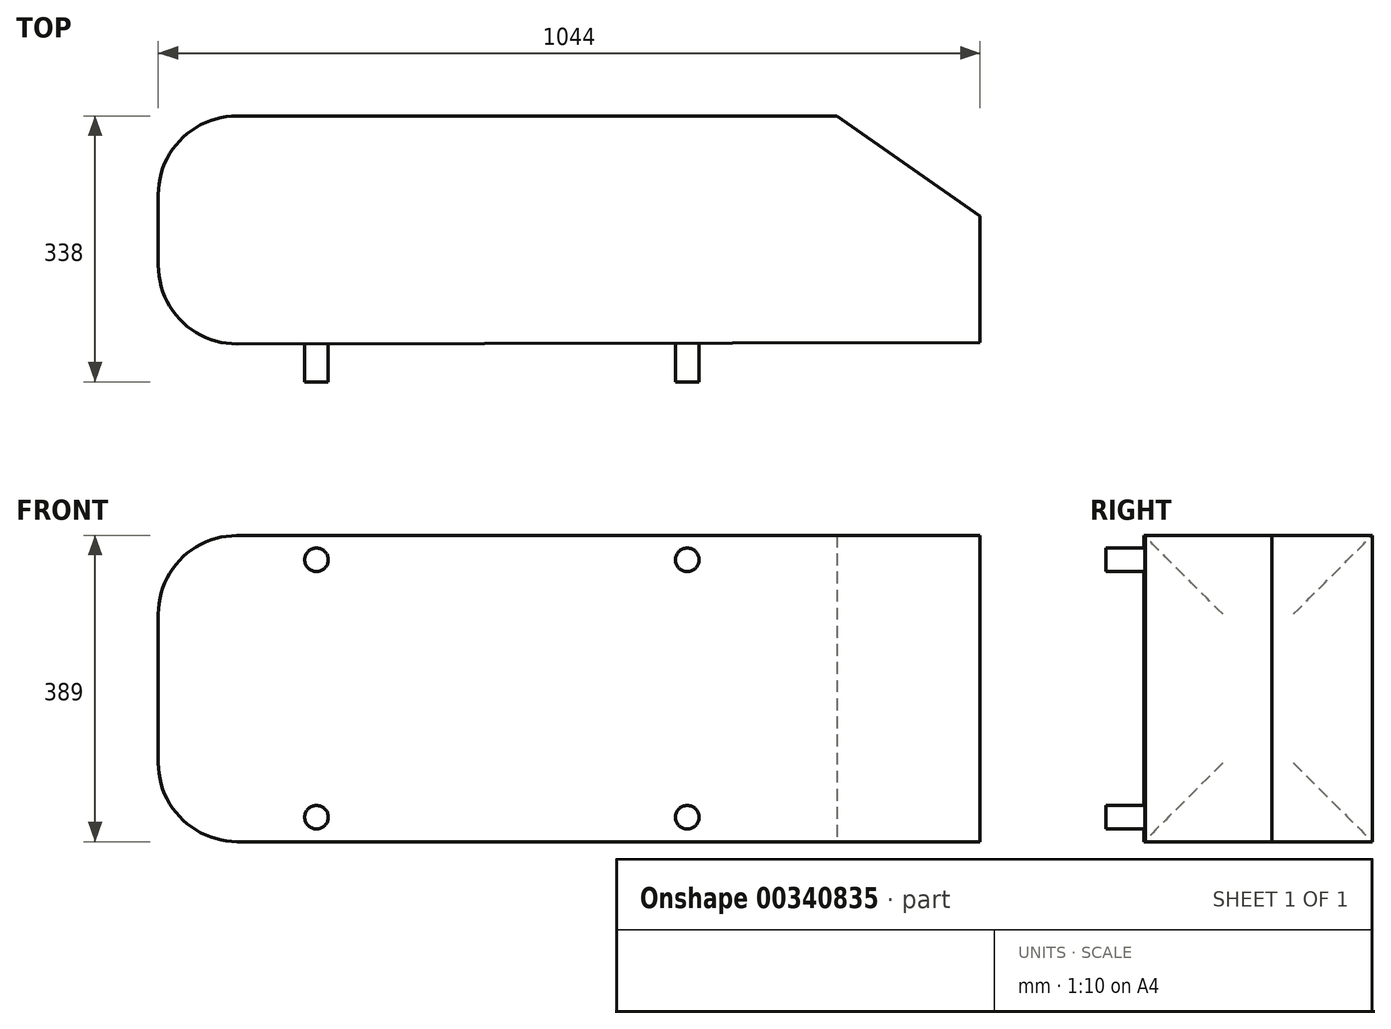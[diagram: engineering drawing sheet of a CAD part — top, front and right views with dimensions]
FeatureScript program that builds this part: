
annotation { "Feature Type Name" : "Feature", "Feature Type Description" : "" }
export const myFeature = defineFeature(function(context is Context, id is Id, definition is map)
    precondition{}
    {
        {
            var Q0;
            Q0=qCreatedBy(makeId("Top.planeOp"),FACE);
            var sketch = newSketch(context, id + "F0", { "sketchPlane" : qUnion([Q0])});
            skLineSegment(sketch, "E0", {"start": v(0, 0) * mm, "end": v(0, 50) * mm, "construction": true});
            skLineSegment(sketch, "E1", {"start": v(0, 50) * mm, "end": v(-1044, 48) * mm});
            skLineSegment(sketch, "E2", {"start": v(-1044, 48) * mm, "end": v(-1044, 50) * mm});
            skLineSegment(sketch, "E3", {"start": v(-1044, 50) * mm, "end": v(-1044, 338) * mm});
            skLineSegment(sketch, "E4", {"start": v(0, 50) * mm, "end": v(0, 210.67) * mm});
            skLineSegment(sketch, "E5", {"start": v(-1044, 338) * mm, "end": v(269.2, 338) * mm, "construction": true});
            skLineSegment(sketch, "E6", {"start": v(-1044, 338) * mm, "end": v(-181.85, 338) * mm});
            skLineSegment(sketch, "E7", {"start": v(0, 210.67) * mm, "end": v(-181.85, 338) * mm});
            skSolve(sketch);
        }
        {
            var Q0;
            Q0=makeQuery(id+"F0.imprint","IMPRINT",FACE,{"disambiguationData":[TD([[makeQuery(id+"F0.imprint","IMPRINT",EDGE,{"derivedFrom":sQuery(id+"F0.wireOp",EDGE,"E1")}),-1.0]])]});
            extrude(context, id + "F1", {"entities" : qUnion([Q0]), "depth" : (389 / 2) * mm});
        }
        {
            var Q0;
            Q0=qSketchRegion(id+"F0",true);
            extrude(context, id + "F2", {"entities" : qUnion([Q0]), "operationType" : NewBodyOperationType.ADD, "oppositeDirection" : true, "depth" : (389 / 2) * mm});
        }
        {
            var Q0;
            Q0=qCreatedBy(makeId("Front.planeOp"),FACE);
            var sketch = newSketch(context, id + "F3", { "sketchPlane" : qUnion([Q0])});
            skLineSegment(sketch, "E8", {"start": v(0, 0) * mm, "end": v(-372, 0) * mm, "construction": true});
            skLineSegment(sketch, "E9", {"start": v(-372, 0) * mm, "end": v(-843, 0) * mm, "construction": true});
            skLineSegment(sketch, "E10", {"start": v(-843, 0) * mm, "end": v(-843, -163.5) * mm, "construction": true});
            skLineSegment(sketch, "E11.MirrorCS", {"start": v(-843, 0) * mm, "end": v(-843, 163.5) * mm, "construction": true});
            skLineSegment(sketch, "E12", {"start": v(-372, 0) * mm, "end": v(-372, -163.5) * mm, "construction": true});
            skLineSegment(sketch, "E13.MirrorCS", {"start": v(-372, 0) * mm, "end": v(-372, 163.5) * mm, "construction": true});
            skCircle(sketch, "E14", {"center": v(-843, 163.5) * mm, "radius": 15 * mm});
            skCircle(sketch, "E15.MirrorC", {"center": v(-843, -163.5) * mm, "radius": 15 * mm});
            skCircle(sketch, "E16", {"center": v(-372, 163.5) * mm, "radius": 15 * mm});
            skCircle(sketch, "E17.MirrorC", {"center": v(-372, -163.5) * mm, "radius": 15 * mm});
            skSolve(sketch);
        }
        {
            var Q0;
            Q0=qSketchRegion(id+"F3",true);
            extrude(context, id + "F4", {"entities" : qUnion([Q0]), "endBound" : BoundingType.UP_TO_NEXT, "oppositeDirection" : true, "depth" : 25 * mm});
        }
        {
            var Q0;
            {var subQ0=sQuery(id+"F0.wireOp",EDGE,"E3");var subQ1=sQuery(id+"F0.wireOp",EDGE,"E2");Q0=makeQuery(id+"F2.boolean.opBoolean","MERGE",FACE,{"derivedFrom":[makeQuery(id+"F1.opExtrude","SWEPT_FACE",FACE,{"disambiguationData":[OSD([subQ1,subQ0])]}),makeQuery(id+"F2.opExtrude","SWEPT_FACE",FACE,{"disambiguationData":[OSD([subQ1,subQ0])]})]});}
            fillet(context, id + "F5", {"entities" : qUnion([Q0]), "radius" : 100 * mm, "tangentPropagation" : true, "allowEdgeOverflow" : false});
        }
    });
